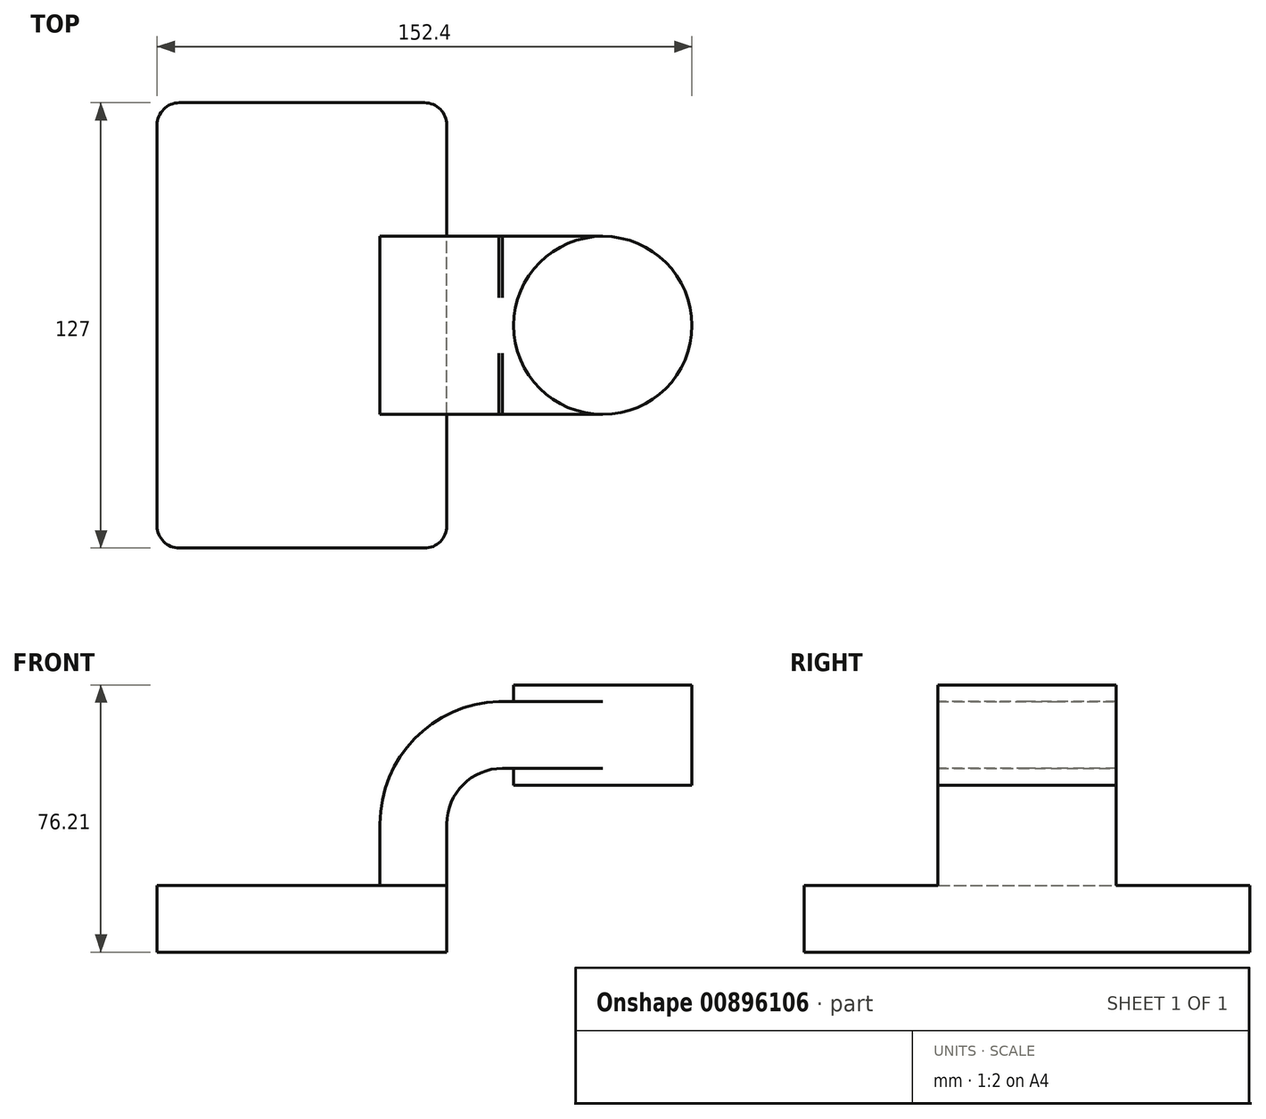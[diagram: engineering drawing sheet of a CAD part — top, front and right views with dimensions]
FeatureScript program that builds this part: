
annotation { "Feature Type Name" : "Feature", "Feature Type Description" : "" }
export const myFeature = defineFeature(function(context is Context, id is Id, definition is map)
    precondition{}
    {
        {
            var Q0;
            Q0=qCreatedBy(makeId("Front.planeOp"),FACE);
            var sketch = newSketch(context, id + "F0", { "sketchPlane" : qUnion([Q0])});
            skLineSegment(sketch, "E0.bottom", {"start": v(-41.28, 9.52) * mm, "end": v(41.28, 9.53) * mm});
            skLineSegment(sketch, "E0.top", {"start": v(-41.28, -9.53) * mm, "end": v(41.28, -9.53) * mm});
            skLineSegment(sketch, "E0.left", {"start": v(-41.28, 9.52) * mm, "end": v(-41.28, -9.53) * mm});
            skLineSegment(sketch, "E0.right", {"start": v(41.28, 9.53) * mm, "end": v(41.28, -9.52) * mm});
            skPoint(sketch, "E0.middle", {"position": v(0, 0) * mm});
            skLineSegment(sketch, "E1", {"start": v(41.27, 9.53) * mm, "end": v(41.27, 27) * mm});
            skLineSegment(sketch, "E2.bottom", {"start": v(60.32, 66.67) * mm, "end": v(111.12, 66.67) * mm});
            skLineSegment(sketch, "E2.top", {"start": v(60.32, 38.1) * mm, "end": v(111.12, 38.1) * mm});
            skLineSegment(sketch, "E2.left", {"start": v(60.32, 66.67) * mm, "end": v(60.32, 38.1) * mm});
            skLineSegment(sketch, "E2.right", {"start": v(111.12, 66.67) * mm, "end": v(111.12, 38.1) * mm});
            skPoint(sketch, "E2.middle", {"position": v(85.72, 52.39) * mm});
            skArc(sketch, "E3", {"start": v(41.27, 27) * mm, "mid": v(45.92, 38.23) * mm, "end": v(57.15, 42.88) * mm});
            skLineSegment(sketch, "E4", {"start": v(57.15, 42.88) * mm, "end": v(85.72, 42.88) * mm});
            skLineSegment(sketch, "E5.0", {"start": v(57.15, 61.93) * mm, "end": v(85.72, 61.93) * mm});
            skArc(sketch, "E5.1", {"start": v(22.23, 27) * mm, "mid": v(32.45, 51.7) * mm, "end": v(57.15, 61.93) * mm});
            skLineSegment(sketch, "E5.2", {"start": v(22.22, 9.53) * mm, "end": v(22.22, 27) * mm});
            skLineSegment(sketch, "E6", {"start": v(85.72, 38.1) * mm, "end": v(85.72, 66.67) * mm});
            skFitSpline(sketch, "E7", {"points": [v(-41.28, 9.52) * mm, v(57.15, 61.93) * mm], "startDerivative": vector(-0.12, 102.45) * mm, "endDerivative": vector(130.3, 1.5) * mm});
            skSolve(sketch);
        }
        {
            var Q0;
            Q0=makeQuery(id+"F0.imprint","IMPRINT",FACE,{"disambiguationData":[TD([[makeQuery(id+"F0.imprint","IMPRINT",EDGE,{"derivedFrom":sQuery(id+"F0.wireOp",EDGE,"E0.top")}),1.0]])]});
            extrude(context, id + "F1", {"entities" : qUnion([Q0]), "endBound" : BoundingType.SYMMETRIC, "depth" : 127 * mm, "offsetDistance" : 25.4 * mm});
        }
        {
            var Q0;
            {var subQ1=sQuery(id+"F0.wireOp",EDGE,"E1");Q0=makeQuery(id+"F0.imprint","IMPRINT",FACE,{"disambiguationData":[TD([[makeQuery(id+"F0.imprint","IMPRINT",EDGE,{"derivedFrom":subQ1}),1.0]])]});}
            var Q1;
            {var subQ0=sQuery(id+"F0.wireOp",EDGE,"E5.0");var subQ1=sQuery(id+"F0.wireOp",EDGE,"E2.left");var subQ2=makeQuery(id+"F0.imprint","INTERSECT",VERTEX,{"derivedFrom":[subQ1,subQ0]});Q1=makeQuery(id+"F0.imprint","IMPRINT",FACE,{"disambiguationData":[TD([[makeQuery(id+"F0.imprint","IMPRINT",EDGE,{"disambiguationData":[TD([[subQ2,-1.0]])],"derivedFrom":subQ1}),1.0]])]});}
            extrude(context, id + "F2", {"entities" : qUnion([Q0, Q1]), "operationType" : NewBodyOperationType.ADD, "endBound" : BoundingType.SYMMETRIC, "depth" : 50.8 * mm, "offsetDistance" : 25.4 * mm});
        }
        {
            var Q0;
            Q0=makeQuery(id+"F0.imprint","IMPRINT",FACE,{"disambiguationData":[TD([[makeQuery(id+"F0.imprint","IMPRINT",EDGE,{"derivedFrom":sQuery(id+"F0.wireOp",EDGE,"E5.1")}),1.0]])]});
            extrude(context, id + "F3", {"entities" : qUnion([Q0]), "operationType" : NewBodyOperationType.ADD, "endBound" : BoundingType.SYMMETRIC, "depth" : 15.88 * mm, "offsetDistance" : 25.4 * mm});
        }
        {
            var Q0;
            {var subQ0=sQuery(id+"F0.wireOp",EDGE,"E2.right");Q0=makeQuery(id+"F0.imprint","IMPRINT",FACE,{"disambiguationData":[TD([[makeQuery(id+"F0.imprint","IMPRINT",EDGE,{"derivedFrom":subQ0}),-1.0]])]});}
            var Q1;
            Q1=sQuery(id+"F0.wireOp",EDGE,"E6");
            revolve(context, id + "F4", {"operationType" : NewBodyOperationType.ADD, "surfaceOperationType" : NewSurfaceOperationType.NEW, "entities" : qUnion([Q0]), "axis" : qUnion([Q1]), "revolveType" : RevolveType.FULL});
        }
        {
            var Q0;
            Q0=makeQuery(id+"F1.opExtrude","CAP_EDGE",EDGE,{"disambiguationData":[OSD([sQuery(id+"F0.wireOp",EDGE,"E0.right")])],"isStart":false});
            var Q1;
            Q1=makeQuery(id+"F1.opExtrude","CAP_EDGE",EDGE,{"disambiguationData":[OSD([sQuery(id+"F0.wireOp",EDGE,"E0.left")])],"isStart":false});
            var Q2;
            Q2=makeQuery(id+"F1.opExtrude","CAP_EDGE",EDGE,{"disambiguationData":[OSD([sQuery(id+"F0.wireOp",EDGE,"E0.left")])],"isStart":true});
            var Q3;
            Q3=makeQuery(id+"F1.opExtrude","CAP_EDGE",EDGE,{"disambiguationData":[OSD([sQuery(id+"F0.wireOp",EDGE,"E0.right")])],"isStart":true});
            fillet(context, id + "F5", {"entities" : qUnion([Q0, Q1, Q2, Q3]), "radius" : 6.35 * mm, "tangentPropagation" : true, "allowEdgeOverflow" : false});
        }
    });
